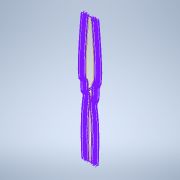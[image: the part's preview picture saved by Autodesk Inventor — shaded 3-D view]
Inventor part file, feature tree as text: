
AUTODESK INVENTOR PART (.ipt)
format: ipt  version: 2022 (Build 260153000, 153)  size: 4,750,336 bytes
history: native  units: mm
features: sketch x10, other x6, surface_op x4, sweep x2
ambient origin geometry x8: Origin, YZ Plane, XZ Plane, XY Plane, X Axis, Y Axis, Z Axis, Center Point
bodies: Body1 (feature_tree), Body2 (feature_tree), Body3 (feature_tree), Body4 (feature_tree), Body5 (feature_tree), Body6 (feature_tree), Body7 (feature_tree), Body8 (feature_tree), Body9 (feature_tree), Body10 (feature_tree), Body11 (feature_tree), Body12 (feature_tree), Body13 (feature_tree), Body14 (feature_tree), Body15 (feature_tree), Body16 (feature_tree), Body17 (feature_tree), Body18 (feature_tree), Body19 (feature_tree), Body20 (feature_tree), Body21 (feature_tree), Body22 (feature_tree), Body23 (feature_tree), Body24 (feature_tree), Body25 (feature_tree), Body26 (feature_tree), Body27 (feature_tree), Body28 (feature_tree), Body29 (feature_tree), Body30 (feature_tree), Body31 (feature_tree), Body32 (feature_tree), Body33 (feature_tree), Body34 (feature_tree), Body35 (feature_tree), Body36 (feature_tree), Body37 (feature_tree), Body38 (feature_tree), Body39 (feature_tree), Body40 (feature_tree), Body41 (feature_tree), Body42 (feature_tree), Body43 (feature_tree), Body44 (feature_tree), Body45 (feature_tree), Body46 (feature_tree), Body47 (feature_tree), Body48 (feature_tree), Body49 (feature_tree), Body50 (feature_tree), Body51 (feature_tree), Body52 (feature_tree), Body53 (feature_tree), Body54 (feature_tree), Body55 (feature_tree), Body56 (feature_tree), Body57 (feature_tree), Body58 (feature_tree), Body59 (feature_tree), Body60 (feature_tree), Body61 (feature_tree), Body62 (feature_tree), Body63 (feature_tree), Body64 (feature_tree), Body65 (feature_tree), Body66 (feature_tree), Body67 (feature_tree), Body68 (feature_tree)
feature tree (22):
  sketch  "Sketch1"  dims[d0=330.0mm d1=90.0deg]
  sketch  "3D Sketch3"
  sketch  "3D Sketch4"
  surface_op  "Stitch Surface1"
  sketch  "3D Sketch5"
  surface_op  "Stitch Surface2"
  sketch  "3D Sketch1"
  sketch  "Sketch2"  dims[d2=0.0mm d3=0.0mm d4=330.0mm]
  other  "Srf1"
  sketch  "3D Sketch2"
  sketch  "Sketch3"  dims[d5=90.0deg d6=0.0mm d7=0.0mm d16=0.0mm d17=5.0mm d18=0.0mm]
  other  "Srf2"
  other  "Srf4"
  sketch  "3D Sketch6"
  sketch  "3D Sketch7"
  other  "Srf8"
  other  "Srf9"
  other  "Srf10"
  sweep  "SweepSrf1"
  sweep  "SweepSrf2"
  surface_op  "Boundary Patch5"
  surface_op  "Boundary Patch6"
